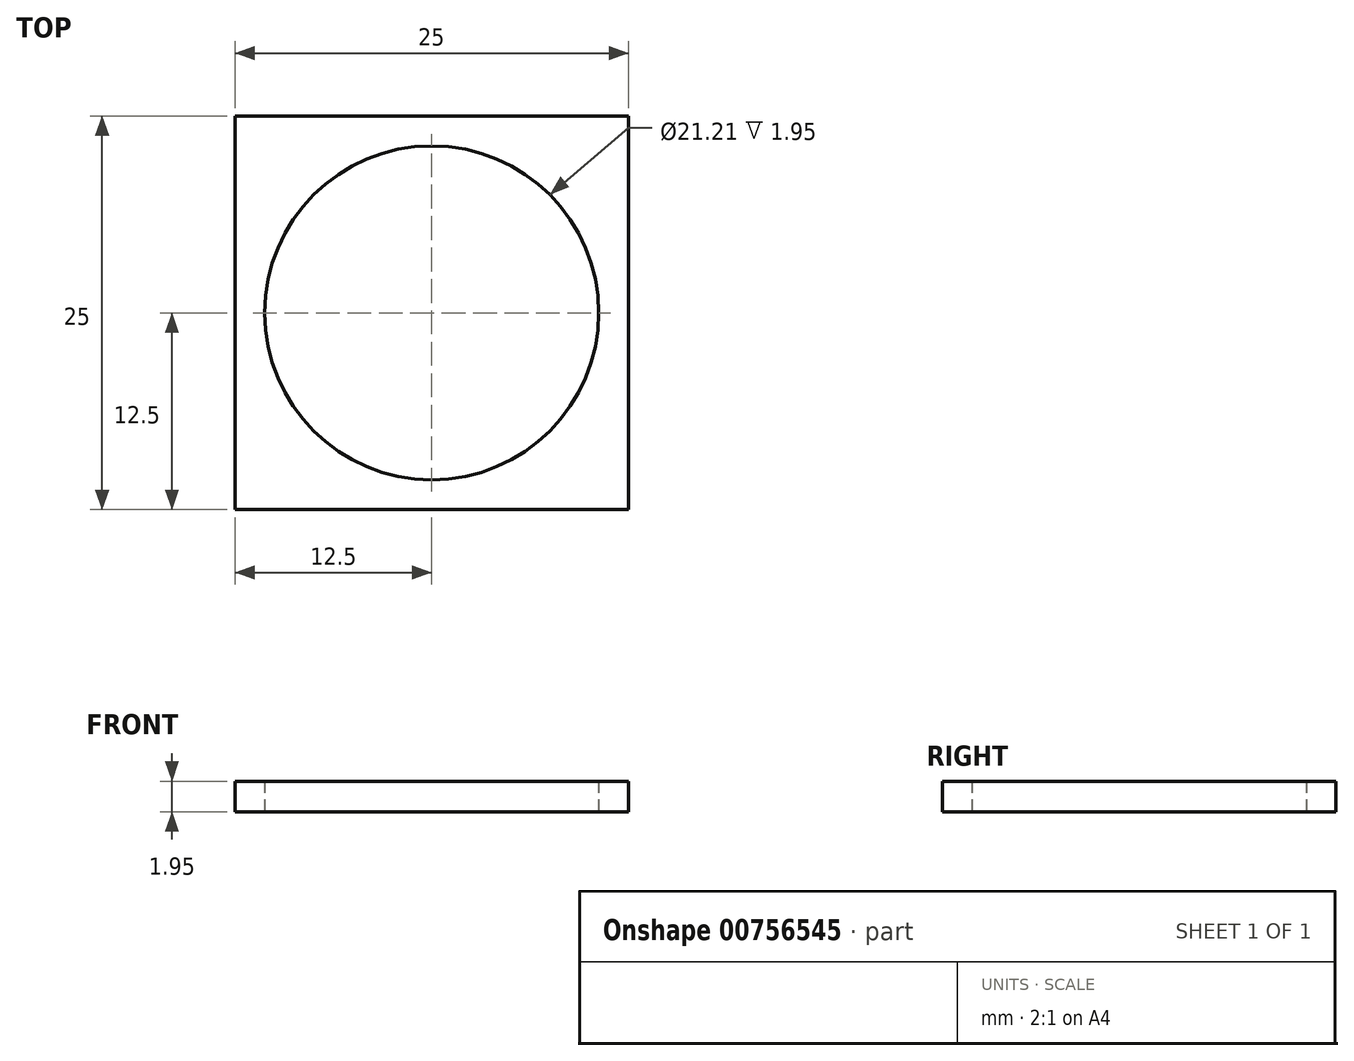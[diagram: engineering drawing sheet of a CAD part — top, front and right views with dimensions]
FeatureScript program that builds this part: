
annotation { "Feature Type Name" : "Feature", "Feature Type Description" : "" }
export const myFeature = defineFeature(function(context is Context, id is Id, definition is map)
    precondition{}
    {
        {
            var Q0;
            Q0=qCreatedBy(makeId("Top.planeOp"),FACE);
            var sketch = newSketch(context, id + "F0", { "sketchPlane" : qUnion([Q0])});
            skLineSegment(sketch, "E0.bottom", {"start": v(-12.5, 12.5) * mm, "end": v(12.5, 12.5) * mm});
            skLineSegment(sketch, "E0.top", {"start": v(-12.5, -12.5) * mm, "end": v(12.5, -12.5) * mm});
            skLineSegment(sketch, "E0.left", {"start": v(-12.5, 12.5) * mm, "end": v(-12.5, -12.5) * mm});
            skLineSegment(sketch, "E0.right", {"start": v(12.5, 12.5) * mm, "end": v(12.5, -12.5) * mm});
            skCircle(sketch, "E1", {"center": v(0, 0) * mm, "radius": 10.6 * mm});
            skPoint(sketch, "E2", {"position": v(-12.5, 0) * mm});
            skPoint(sketch, "E3", {"position": v(0, -12.5) * mm});
            skSolve(sketch);
        }
        {
            var Q0;
            Q0=makeQuery(id+"F0.imprint","IMPRINT",FACE,{"disambiguationData":[TD([[makeQuery(id+"F0.imprint","IMPRINT",EDGE,{"derivedFrom":sQuery(id+"F0.wireOp",EDGE,"E0.bottom")}),-1.0]])]});
            extrude(context, id + "F1", {"entities" : qUnion([Q0]), "depth" : 1.95 * mm, "offsetDistance" : 25.4 * mm});
        }
    });
